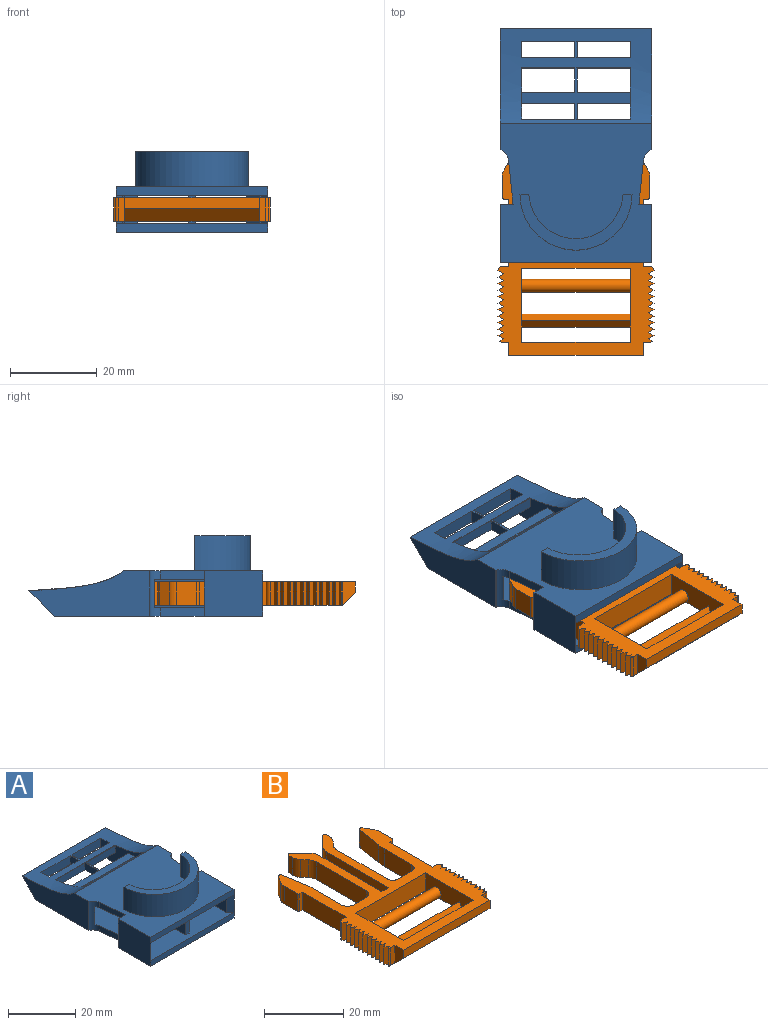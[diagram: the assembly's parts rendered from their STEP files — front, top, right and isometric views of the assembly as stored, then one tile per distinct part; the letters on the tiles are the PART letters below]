
ASSEMBLY  parts=2 mates=1
PART A: 63 faces, bbox 35x54x18.6 mm
  f0: plane 3.75x0.5mm, normal (0,0.06,1), area 1.9mm2, adj f2,f3,f37
  f1: plane 3.75x1mm, normal (0,-0.26,-0.97), area 1.9mm2, adj f2,f3,f7,f38
  f2: plane 3.75x3.3mm, normal (1,0,0), area 10.1mm2, adj f0,f1,f5,f28
  f3: plane 3.75x3.3mm, normal (-1,0,0), area 10.1mm2, adj f0,f1,f4,f29
  f4: plane 12.25x3.07mm, normal (0,-1,0), area 37.6mm2, adj f3,f26,f37,f38
  f5: plane 12.25x2.3mm, normal (0,1,0), area 28.1mm2, adj f2,f7,f25,f37
  f6: plane 25x11.93mm, normal (0,0,1), area 71.7mm2, adj f8,f9,f10,f11,f12,f13,f25,f26
  f7: plane 25x14.25mm, normal (0,0,-1), area 129.6mm2, adj f1,f5,f8,f9,f10,f11,f12,f13
  f8: plane 5.5x2.5mm, normal (1,0,0), area 13.7mm2, adj f6,f7,f10,f11
  f9: plane 5.5x2.5mm, normal (-1,0,0), area 13.7mm2, adj f6,f7,f34,f35
  f10: plane 12.25x2.5mm, normal (0,-1,0), area 30.6mm2, adj f6,f7,f8,f25
  f11: plane 12.25x2.5mm, normal (0,1,0), area 30.6mm2, adj f6,f7,f8,f25
  f12: plane 12.25x2.5mm, normal (0,-1,0), area 30.6mm2, adj f6,f7,f25,f56
  f13: plane 25x9.83mm, normal (0,1,0), area 91mm2, adj f6,f7,f20,f21,f23,f25,f26,f37
  f14: plane 35x2mm, normal (0,-1,0), area 70mm2, adj f17,f18,f20,f21
  f15: plane 6.5x0.4mm, normal (0,-1,0), area 2.6mm2, adj f21,f23,f31,f53
  f16: plane 27.93x10.5mm, normal (1,0,0), area 202mm2, adj f19,f20,f37,f38,f44
  f17: plane 13.5x10.5mm, normal (1,0,0), area 141.8mm2, adj f14,f19,f20,f30,f48,f54
  f18: plane 13.5x10.5mm, normal (-1,0,0), area 141.8mm2, adj f14,f19,f20,f30,f42,f55
  f19: plane 35x32.08mm, normal (0,0,1), area 976.6mm2, adj f16,f17,f18,f27,f30,f37,f40,f41
  f20: plane 48x35mm, normal (0,0,-1), area 1248.5mm2, adj f13,f14,f16,f17,f18,f25,f26,f27
  f21: plane 35x33mm, normal (0,0,1), area 969.2mm2, adj f13,f14,f15,f22,f24,f25,f26,f31
  f22: plane 12x6.5mm, normal (-1,0,0), area 78mm2, adj f21,f23,f48,f54
  f23: plane 35x33mm, normal (0,0,-1), area 969.2mm2, adj f13,f15,f22,f24,f25,f26,f30,f31
  f24: plane 6.5x3.15mm, normal (1,0,0), area 20.5mm2, adj f21,f23,f33,f41
  f25: plane 19.91x10.02mm, normal (-1,0,0), area 125.2mm2, adj f5,f6,f7,f10,f11,f12,f13,f20
  f26: plane 19.91x10.02mm, normal (1,0,0), area 125.2mm2, adj f4,f6,f7,f13,f20,f21,f23,f29
  f27: plane 27.93x10.5mm, normal (-1,0,0), area 202mm2, adj f19,f20,f37,f38,f43
  f28: plane 12.25x3.07mm, normal (0,-1,0), area 37.6mm2, adj f2,f25,f37,f38
  f29: plane 12.25x2.3mm, normal (0,1,0), area 28.1mm2, adj f3,f7,f26,f37
  f30: plane 35x2mm, normal (0,-1,0), area 70mm2, adj f17,f18,f19,f23
  f31: plane 6.5x3.15mm, normal (-1,0,0), area 20.5mm2, adj f15,f21,f23,f45
  f32: plane 12x6.5mm, normal (1,0,0), area 78mm2, adj f21,f23,f42,f55
  f33: plane 6.5x0.4mm, normal (0,-1,0), area 2.6mm2, adj f21,f23,f24,f52
  f34: plane 12.25x2.5mm, normal (0,-1,0), area 30.6mm2, adj f6,f7,f9,f26
  f35: plane 12.25x2.5mm, normal (0,1,0), area 30.6mm2, adj f6,f7,f9,f26
  f36: plane 12.25x2.5mm, normal (0,-1,0), area 30.6mm2, adj f6,f7,f26,f57
  f37: extruded ~35x21.85mm, area 386.4mm2, adj f0,f4,f5,f6,f13,f16,f19,f25
  f38: plane 35x5.92mm, normal (0,0.71,-0.71), area 187.2mm2, adj f1,f4,f16,f20,f25,f26,f27,f28
  f39: plane 10.07x2mm, normal (-0.99,-0.1,0), area 20.2mm2, adj f20,f21,f41,f42
  f40: plane 10.07x2mm, normal (-0.99,-0.1,0), area 20.2mm2, adj f19,f23,f41,f42
  f41: cylinder r=3mm len=10.5mm, axis (0,0,1), area 24.6mm2, adj f19,f20,f21,f23,f24,f39,f40,f43
  f42: plane 10.5x3mm, normal (0,1,0), area 21.8mm2, adj f18,f19,f20,f21,f23,f32,f39,f40
  f43: plane 10.5x0.14mm, normal (-0.39,-0.92,0), area 1.6mm2, adj f19,f20,f27,f41
  f44: plane 10.5x0.14mm, normal (0.39,-0.92,0), area 1.6mm2, adj f16,f19,f20,f45
  f45: cylinder r=3mm len=10.5mm, axis (0,0,1), area 24.6mm2, adj f19,f20,f21,f23,f31,f44,f46,f47
  f46: plane 10.07x2mm, normal (0.99,-0.1,0), area 20.2mm2, adj f20,f21,f45,f48
  f47: plane 10.07x2mm, normal (0.99,-0.1,0), area 20.2mm2, adj f19,f23,f45,f48
  f48: plane 10.5x3mm, normal (0,1,0), area 21.8mm2, adj f17,f19,f20,f21,f22,f23,f46,f47
  f49: plane 31x6.5mm, normal (-1,0,0), area 201.5mm2, adj f13,f21,f23,f51
  f50: plane 31x6.5mm, normal (1,0,0), area 201.5mm2, adj f13,f21,f23,f51
  f51: plane 6.5x1.4mm, normal (0,-1,0), area 9.1mm2, adj f21,f23,f49,f50
  f52: plane 6.5x3.1mm, normal (0.71,-0.71,0), area 28.5mm2, adj f21,f23,f26,f33
  f53: plane 6.5x3.1mm, normal (-0.71,-0.71,0), area 28.5mm2, adj f15,f21,f23,f25
  f54: plane 6.5x1.5mm, normal (-0.71,-0.71,0), area 13.8mm2, adj f17,f21,f22,f23
  f55: plane 6.5x1.5mm, normal (0.71,-0.71,0), area 13.8mm2, adj f18,f21,f23,f32
  f56: plane 3.75x2.5mm, normal (1,0,0), area 9.4mm2, adj f6,f7,f12,f13
  f57: plane 3.75x2.5mm, normal (-1,0,0), area 9.4mm2, adj f6,f7,f13,f36
  f58: plane 8.1x2.04mm, normal (0,1,0), area 16.5mm2, adj f19,f59,f61,f62
  f59: cylinder r=12.92mm len=25.84mm, axis (0,0,-1), area 328.7mm2, adj f19,f58,f60,f62
  f60: plane 8.1x2.07mm, normal (0,1,0), area 16.8mm2, adj f19,f59,f61,f62
  f61: cylinder r=10.88mm len=21.72mm, axis (0,0,-1), area 266.8mm2, adj f19,f58,f60,f62
  f62: plane 25.84x12.92mm, normal (0,0,1), area 89.6mm2, adj f58,f59,f60,f61
PART B: 110 faces, bbox 36x50.4x5.5 mm
  f0: plane 5.5x3mm, normal (-1,0,0), area 12mm2, adj f2,f53,f57,f84
  f1: plane 5.5x3mm, normal (1,0,0), area 12mm2, adj f2,f53,f57,f58
  f2: plane 31x2.5mm, normal (0,-1,0), area 77.5mm2, adj f0,f1,f53,f57
  f3: plane 47.42x36mm, normal (0,0,-1), area 618.6mm2, adj f4,f6,f7,f8,f9,f10,f11,f12
  f4: plane 17x5.5mm, normal (-1,0,0), area 82.5mm2, adj f3,f5,f52,f53,f54,f55,f56
  f5: plane 25x5.5mm, normal (0,1,0), area 137.5mm2, adj f4,f6,f53,f57
  f6: plane 17x5.5mm, normal (1,0,0), area 82.5mm2, adj f3,f5,f52,f53,f54,f55,f56
  f7: plane 5.5x2.4mm, normal (0,1,0), area 13.2mm2, adj f3,f8,f51,f53
  f8: plane 22.52x5.5mm, normal (1,0,0), area 123.9mm2, adj f3,f7,f9,f53
  f9: cylinder r=3mm len=5.5mm, axis (0,0,-1), area 13mm2, adj f3,f8,f10,f53
  f10: plane 5.5x3.63mm, normal (0.71,0.71,0), area 28.2mm2, adj f3,f9,f11,f53
  f11: cylinder r=0.5mm len=5.5mm, axis (0,0,-1), area 6.5mm2, adj f3,f10,f12,f53
  f12: plane 5.5x1.43mm, normal (-1,0,0), area 7.8mm2, adj f3,f11,f13,f53
  f13: cylinder r=3mm len=5.5mm, axis (0,0,-1), area 12mm2, adj f3,f12,f14,f53
  f14: plane 5.5x1.49mm, normal (-0.75,-0.67,0), area 11mm2, adj f3,f13,f15,f53
  f15: cylinder r=3mm len=5.5mm, axis (0,0,-1), area 12mm2, adj f3,f14,f16,f53
  f16: plane 18x5.5mm, normal (-1,0,0), area 99mm2, adj f3,f15,f17,f53
  f17: cylinder r=2mm len=5.5mm, axis (0,0,-1), area 17.3mm2, adj f3,f16,f18,f53
  f18: plane 5.5x4.8mm, normal (0,1,0), area 26.4mm2, adj f3,f17,f19,f53
  f19: cylinder r=2mm len=5.5mm, axis (0,0,-1), area 17.3mm2, adj f3,f18,f20,f53
  f20: plane 9.84x5.5mm, normal (1,0,0), area 54.1mm2, adj f3,f19,f21,f53
  f21: cylinder r=15mm len=5.5mm, axis (0,0,-1), area 12.7mm2, adj f3,f20,f22,f53
  f22: plane 7.76x5.5mm, normal (0.99,0.15,0), area 43.2mm2, adj f3,f21,f23,f53
  f23: cylinder r=0.7mm len=5.5mm, axis (0,0,-1), area 9.5mm2, adj f3,f22,f24,f53
  f24: plane 5.5x2.45mm, normal (-0.87,0.5,0), area 15.6mm2, adj f3,f23,f25,f53
  f25: cylinder r=3mm len=5.5mm, axis (0,0,-1), area 8.6mm2, adj f3,f24,f26,f53
  f26: plane 5.5x4.7mm, normal (-1,0,0), area 25.8mm2, adj f3,f25,f27,f53
  f27: cylinder r=0.5mm len=5.5mm, axis (0,0,-1), area 4.3mm2, adj f3,f26,f28,f53
  f28: plane 5.5x1mm, normal (0,-1,0), area 5.5mm2, adj f3,f27,f29,f53
  f29: plane 15.5x5.5mm, normal (-1,0,0), area 85.2mm2, adj f3,f28,f53,f87
  f30: plane 15.5x5.5mm, normal (1,0,0), area 85.2mm2, adj f3,f31,f53,f61
  f31: plane 5.5x1mm, normal (0,-1,0), area 5.5mm2, adj f3,f30,f32,f53
  f32: cylinder r=0.5mm len=5.5mm, axis (0,0,-1), area 4.3mm2, adj f3,f31,f33,f53
  f33: plane 5.5x4.7mm, normal (1,0,0), area 25.8mm2, adj f3,f32,f34,f53
  f34: cylinder r=3mm len=5.5mm, axis (0,0,-1), area 8.6mm2, adj f3,f33,f35,f53
  f35: plane 5.5x2.45mm, normal (0.87,0.5,0), area 15.6mm2, adj f3,f34,f36,f53
  f36: cylinder r=0.7mm len=5.5mm, axis (0,0,-1), area 9.5mm2, adj f3,f35,f37,f53
  f37: plane 7.76x5.5mm, normal (-0.99,0.15,0), area 43.2mm2, adj f3,f36,f38,f53
  f38: cylinder r=15mm len=5.5mm, axis (0,0,-1), area 12.7mm2, adj f3,f37,f39,f53
  f39: plane 9.84x5.5mm, normal (-1,0,0), area 54.1mm2, adj f3,f38,f40,f53
  f40: cylinder r=2mm len=5.5mm, axis (0,0,-1), area 17.3mm2, adj f3,f39,f41,f53
  f41: plane 5.5x4.8mm, normal (0,1,0), area 26.4mm2, adj f3,f40,f42,f53
  f42: cylinder r=2mm len=5.5mm, axis (0,0,-1), area 17.3mm2, adj f3,f41,f43,f53
  f43: plane 18x5.5mm, normal (1,0,0), area 99mm2, adj f3,f42,f44,f53
  f44: cylinder r=3mm len=5.5mm, axis (0,0,-1), area 12mm2, adj f3,f43,f45,f53
  f45: plane 5.5x1.49mm, normal (0.75,-0.67,0), area 11mm2, adj f3,f44,f46,f53
  f46: cylinder r=3mm len=5.5mm, axis (0,0,-1), area 12mm2, adj f3,f45,f47,f53
  f47: plane 5.5x1.16mm, normal (1,0,0), area 6.4mm2, adj f3,f46,f48,f53
  f48: cylinder r=0.5mm len=5.5mm, axis (0,0,-1), area 6.5mm2, adj f3,f47,f49,f53
  f49: plane 5.5x3.63mm, normal (-0.71,0.71,0), area 28.2mm2, adj f3,f48,f50,f53
  f50: cylinder r=3mm len=5.5mm, axis (0,0,-1), area 13mm2, adj f3,f49,f51,f53
  f51: plane 22.26x5.5mm, normal (-1,0,0), area 122.4mm2, adj f3,f7,f50,f53
  f52: plane 25x5.5mm, normal (0,-1,0), area 137.5mm2, adj f3,f4,f6,f53
  f53: plane 50.42x36mm, normal (0,0,1), area 636.6mm2, adj f0,f1,f2,f4,f5,f6,f7,f8
  f54: plane 25x2.6mm, normal (0,0.87,0.5), area 75mm2, adj f3,f4,f6,f55
  f55: plane 25x2.6mm, normal (0,-0.87,0.5), area 75mm2, adj f3,f4,f6,f54
  f56: cylinder r=1.5mm len=25mm, axis (-1,0,0), area 235.6mm2, adj f4,f6
  f57: plane 31x3mm, normal (0,-0.71,-0.71), area 131.5mm2, adj f0,f1,f2,f3,f5
  f58: plane 5.5x1.5mm, normal (0,-1,0), area 8.2mm2, adj f1,f3,f53,f59
  f59: cylinder r=1mm len=5.5mm, axis (0,0,1), area 3.7mm2, adj f3,f53,f58,f81
  f60: cylinder r=1mm len=5.5mm, axis (0,0,1), area 8.6mm2, adj f3,f53,f61,f82
  f61: plane 5.5x1.5mm, normal (0,1,0), area 8.2mm2, adj f3,f30,f53,f60
  f62: plane 5.5x1.3mm, normal (0.5,-0.87,0), area 8.2mm2, adj f3,f53,f63,f79
  f63: plane 5.5x1.3mm, normal (0.5,0.87,0), area 8.2mm2, adj f3,f53,f62,f80
  f64: plane 5.5x1.3mm, normal (0.5,-0.87,0), area 8.2mm2, adj f3,f53,f65,f77
  f65: plane 5.5x1.3mm, normal (0.5,0.87,0), area 8.2mm2, adj f3,f53,f64,f78
  f66: plane 5.5x1.3mm, normal (0.5,-0.87,0), area 8.2mm2, adj f3,f53,f67,f75
  f67: plane 5.5x1.3mm, normal (0.5,0.87,0), area 8.2mm2, adj f3,f53,f66,f76
  f68: plane 5.5x1.3mm, normal (0.5,-0.87,0), area 8.2mm2, adj f3,f53,f69,f73
  f69: plane 5.5x1.3mm, normal (0.5,0.87,0), area 8.2mm2, adj f3,f53,f68,f74
  f70: plane 5.5x1.3mm, normal (0.5,-0.87,0), area 8.2mm2, adj f3,f53,f71,f83
  f71: plane 5.5x1.3mm, normal (0.5,0.87,0), area 8.2mm2, adj f3,f53,f70,f72
  f72: plane 5.5x1.3mm, normal (0.5,-0.87,0), area 8.2mm2, adj f3,f53,f71,f73
  f73: plane 5.5x1.3mm, normal (0.5,0.87,0), area 8.2mm2, adj f3,f53,f68,f72
  f74: plane 5.5x1.3mm, normal (0.5,-0.87,0), area 8.2mm2, adj f3,f53,f69,f75
  f75: plane 5.5x1.3mm, normal (0.5,0.87,0), area 8.2mm2, adj f3,f53,f66,f74
  f76: plane 5.5x1.3mm, normal (0.5,-0.87,0), area 8.2mm2, adj f3,f53,f67,f77
  f77: plane 5.5x1.3mm, normal (0.5,0.87,0), area 8.2mm2, adj f3,f53,f64,f76
  f78: plane 5.5x1.3mm, normal (0.5,-0.87,0), area 8.2mm2, adj f3,f53,f65,f79
  f79: plane 5.5x1.3mm, normal (0.5,0.87,0), area 8.2mm2, adj f3,f53,f62,f78
  f80: plane 5.5x1.3mm, normal (0.5,-0.87,0), area 8.2mm2, adj f3,f53,f63,f81
  f81: plane 5.5x0.92mm, normal (0.5,0.87,0), area 5.9mm2, adj f3,f53,f59,f80
  f82: plane 5.5x1.3mm, normal (0.5,-0.87,0), area 8.2mm2, adj f3,f53,f60,f83
  f83: plane 5.5x1.3mm, normal (0.5,0.87,0), area 8.2mm2, adj f3,f53,f70,f82
  f84: plane 5.5x1.5mm, normal (0,-1,0), area 8.2mm2, adj f0,f3,f53,f85
  f85: cylinder r=1mm len=5.5mm, axis (0,0,1), area 3.7mm2, adj f3,f53,f84,f107
  f86: cylinder r=1mm len=5.5mm, axis (0,0,1), area 8.6mm2, adj f3,f53,f87,f108
  f87: plane 5.5x1.5mm, normal (0,1,0), area 8.2mm2, adj f3,f29,f53,f86
  f88: plane 5.5x1.3mm, normal (-0.5,-0.87,0), area 8.2mm2, adj f3,f53,f89,f105
  f89: plane 5.5x1.3mm, normal (-0.5,0.87,0), area 8.2mm2, adj f3,f53,f88,f106
  f90: plane 5.5x1.3mm, normal (-0.5,-0.87,0), area 8.2mm2, adj f3,f53,f91,f103
  f91: plane 5.5x1.3mm, normal (-0.5,0.87,0), area 8.2mm2, adj f3,f53,f90,f104
  f92: plane 5.5x1.3mm, normal (-0.5,-0.87,0), area 8.2mm2, adj f3,f53,f93,f101
  f93: plane 5.5x1.3mm, normal (-0.5,0.87,0), area 8.2mm2, adj f3,f53,f92,f102
  f94: plane 5.5x1.3mm, normal (-0.5,-0.87,0), area 8.2mm2, adj f3,f53,f95,f99
  f95: plane 5.5x1.3mm, normal (-0.5,0.87,0), area 8.2mm2, adj f3,f53,f94,f100
  f96: plane 5.5x1.3mm, normal (-0.5,-0.87,0), area 8.2mm2, adj f3,f53,f97,f109
  f97: plane 5.5x1.3mm, normal (-0.5,0.87,0), area 8.2mm2, adj f3,f53,f96,f98
  f98: plane 5.5x1.3mm, normal (-0.5,-0.87,0), area 8.2mm2, adj f3,f53,f97,f99
  f99: plane 5.5x1.3mm, normal (-0.5,0.87,0), area 8.2mm2, adj f3,f53,f94,f98
  f100: plane 5.5x1.3mm, normal (-0.5,-0.87,0), area 8.2mm2, adj f3,f53,f95,f101
  f101: plane 5.5x1.3mm, normal (-0.5,0.87,0), area 8.2mm2, adj f3,f53,f92,f100
  f102: plane 5.5x1.3mm, normal (-0.5,-0.87,0), area 8.2mm2, adj f3,f53,f93,f103
  f103: plane 5.5x1.3mm, normal (-0.5,0.87,0), area 8.2mm2, adj f3,f53,f90,f102
  f104: plane 5.5x1.3mm, normal (-0.5,-0.87,0), area 8.2mm2, adj f3,f53,f91,f105
  f105: plane 5.5x1.3mm, normal (-0.5,0.87,0), area 8.2mm2, adj f3,f53,f88,f104
  f106: plane 5.5x1.3mm, normal (-0.5,-0.87,0), area 8.2mm2, adj f3,f53,f89,f107
  f107: plane 5.5x0.92mm, normal (-0.5,0.87,0), area 5.9mm2, adj f3,f53,f85,f106
  f108: plane 5.5x1.3mm, normal (-0.5,-0.87,0), area 8.2mm2, adj f3,f53,f86,f109
  f109: plane 5.5x1.3mm, normal (-0.5,0.87,0), area 8.2mm2, adj f3,f53,f96,f108
PLACE A at identity fixed
PLACE B t=(0,-23.97,2.5)mm
MATE slider A.f51 <-> B.f7  axis (0,-1,0) through (0,-25,5.25)mm
